# Revit family: Electronics_Masking-Generators_Biamp_Cambridge_Sound-Masking-Control-Module_QT-X-600_600D__
name_source: partatom
category: Communication Devices
units: mm (PartAtom-declared; Revit-internal decimal feet)

## family parameters
Cut with Voids When Loaded = No
Host = Face
Maintain Annotation Orientation = No
OmniClass Number = 23.85.10.11.11
OmniClass Title = Sound and Signal Devices
Part Type = Normal
Room Calculation Point = No
Round Connector Dimension = Use Diameter
Shared = No

## types (1)
- Qt X 600/600D
    Altitude = 0-10,000 ft (0-3000m) MSL
    Apparent Load = 150 VA
    Audio Input Connector Type = Captive Screw Terminal
    Compliance = FCC Part 15B (USA), UL Listed (USA and Canada), CE Marked (Europe), RoHS Directive (Europe)
    Connector Description = 100-240VAC 50/60Hz
    Current = 1 A
    Default Elevation = 48 "
    Depth = 3.8 "
    Description = Cambridge QT X 600/600D Sound Masking Control Module
    Height = 3.5 "
    Housing Material = Biamp - Metal - Black
    Humidity = 0-95% relative humidity (non-condensing)
    Included Accessories = ACT Hole Saw, Wall Bracket
    Input Gain Range = 6dB steps
    Input Impedance = 8 kohm
    Input Level = +24dBu (12.3VRMS max)
    Input Level Adjustment = 1dB steps
    Manufacturer = Biamp
    Masking Level Adjustment = 0.5dB steps
    Max Emitter Cabling Distance = 800 feet (243m) per cable run (Qt Active Emitters); 1000 feet (300m) per cable run (Qt Emitters)
    Max Emitter/Device Capacity = 50 Qt Active Emitters; 60 Qt Emitters
    Max Power Consumption (24VDC) = 30 W
    Maximum Masking SPL = 55dBA at 1m (Qt Active Emitters); 55dBA at 1m (Qt Emitters)
    Maximum Music/Paging SPL = 74dBA at 1m (Qt Active Emitters); 56dBA at 1m (Qt Emitters)
    Minimum Masking SPL = 30dBA at 1m (Qt Active Emitters); 30dBA at 1m (Qt Emitters)
    Minimum Output Impedance = 2 ohm (per channel)
    Model = Qt X 600/600D
    Music/Paging Equalization = 200Hz - 8kHz: ISO 1/1 Octave Bands (Qt Active Emitters); 200Hz - 8kHz: ISO 1/1 Octave Bands (Qt Emitters)
    Music/Paging Frequency Response = 115Hz to 12kHz (Qt Active Emitters); 200Hz to 10kHz (Qt Emitters)
    Number of Audio Inputs = 2 (Mono)
    Number of Masking Zones = 6 (2 cable runs per zone)
    Number of Non-Correlated Masking Sources = 4 per zone
    Number of Poles = 1
    Number of Remote Control Outputs = 2 Channels GPIO
    Output = 24VDC at 2.7A
    Output Connections = 6 RJ-45
    Phantom Power = +48VDC (7mA/input)
    Power Factor = 1
    Product Documentation Link = https://downloads.biamp.com
    Product Page URL = https://www.biamp.com
    Product data url = https://www.bimobject.com
    Qt X 300/300D = No
    Qt X 600/600D = Yes
    Remote Control Connector Type = Captive Screw Terminal
    Remote Control Input Type = Contact Closure (Normally Open)
    Remote Control Number of Inputs = 2
    Remote Control Output Type = Logic Status (5VDC)
    Sound Maskin Equalization = 125Hz - 6.3kHz: ISO 1/3 Octave Bands (Qt Active Emitters); 200Hz - 6.3kHz: ISO 1/3 Octave Bands (Qt Emitters)
    Sound Masking Frequency Response = 125Hz to 6.3kHz (Qt Active Emitters); 200Hz to 6.3kHz (Qt Emitters)
    Temperature Range = 40 - 104° F (4 – 40° C)
    URL = https://www.biamp.com
    Voltage = 120 V
    Weight = 4.20 lbf
    Width = 14.63 "

## geometry (parser evidence)
native form markers: Sweep x4
no freeform markers — native parametric forms only
